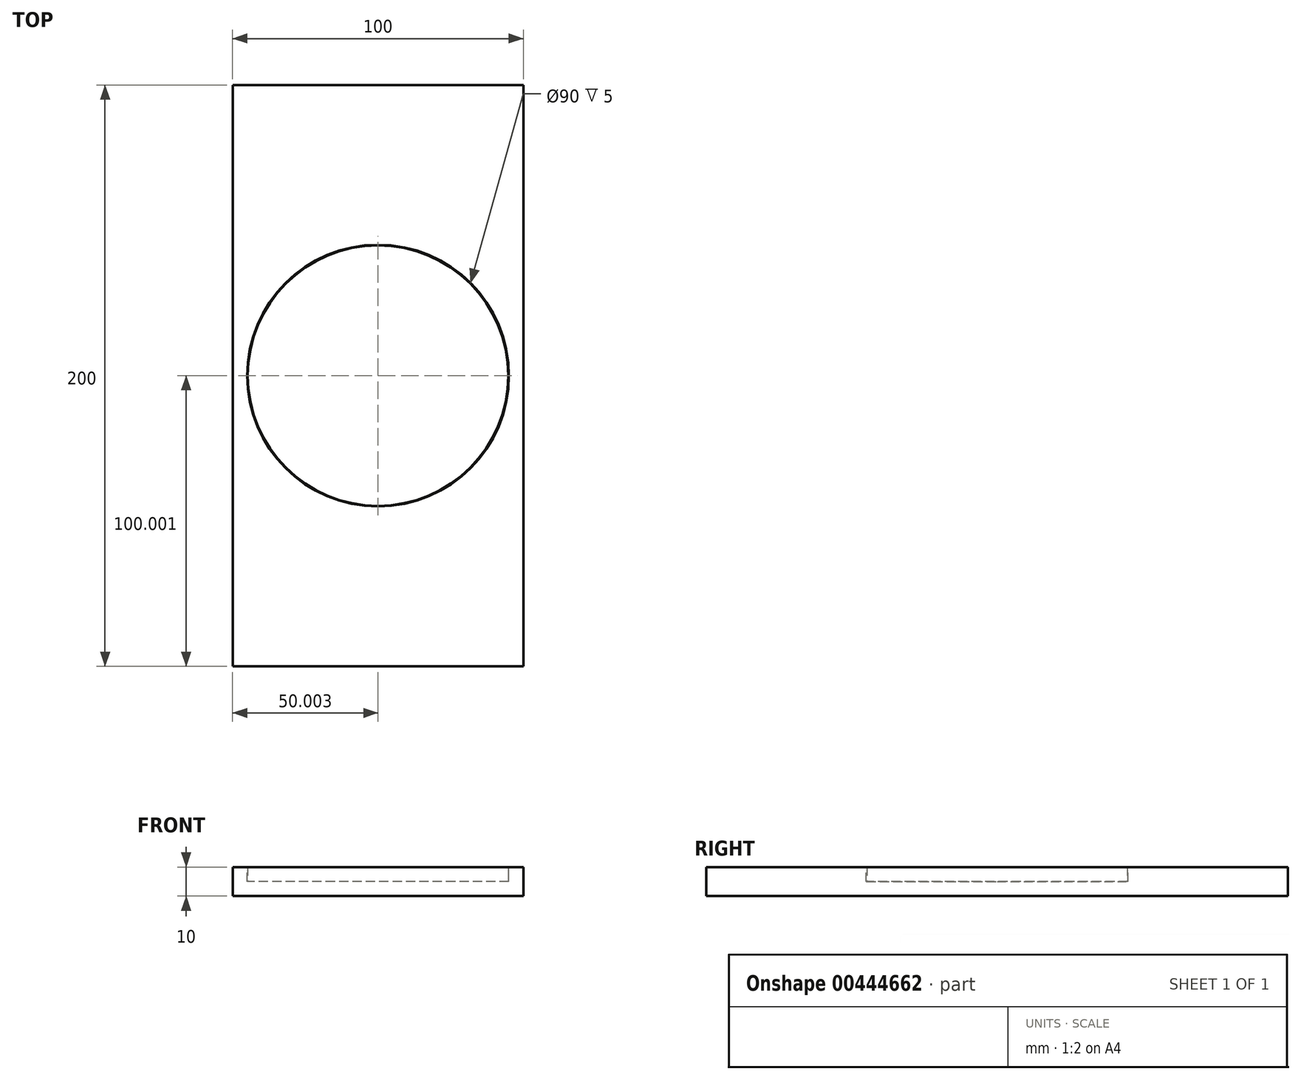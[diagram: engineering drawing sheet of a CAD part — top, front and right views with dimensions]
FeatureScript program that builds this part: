
annotation { "Feature Type Name" : "Feature", "Feature Type Description" : "" }
export const myFeature = defineFeature(function(context is Context, id is Id, definition is map)
    precondition{}
    {
        {
            var Q0;
            Q0=qCreatedBy(makeId("Top.planeOp"),FACE);
            var sketch = newSketch(context, id + "F0", { "sketchPlane" : qUnion([Q0])});
            skLineSegment(sketch, "E0.bottom", {"start": v(-48.37, 154.08) * mm, "end": v(51.63, 154.08) * mm});
            skLineSegment(sketch, "E0.top", {"start": v(-48.37, -45.92) * mm, "end": v(51.63, -45.92) * mm});
            skLineSegment(sketch, "E0.left", {"start": v(-48.37, 154.08) * mm, "end": v(-48.37, -45.92) * mm});
            skLineSegment(sketch, "E0.right", {"start": v(51.63, 154.08) * mm, "end": v(51.63, -45.92) * mm});
            skSolve(sketch);
        }
        {
            var Q0;
            Q0=makeQuery(id+"F0.imprint","IMPRINT",FACE,{"disambiguationData":[TD([[makeQuery(id+"F0.imprint","IMPRINT",EDGE,{"derivedFrom":sQuery(id+"F0.wireOp",EDGE,"E0.bottom")}),-1.0]])]});
            extrude(context, id + "F1", {"entities" : qUnion([Q0]), "depth" : 10 * mm});
        }
        {
            var Q0;
            Q0=makeQuery(id+"F1.opExtrude","CAP_FACE",FACE,{"disambiguationData":[OSD([sQuery(id+"F0.wireOp",EDGE,"E0.bottom"),sQuery(id+"F0.wireOp",EDGE,"E0.top"),sQuery(id+"F0.wireOp",EDGE,"E0.left"),sQuery(id+"F0.wireOp",EDGE,"E0.right")])],"isStart":false});
            var sketch = newSketch(context, id + "F2", { "sketchPlane" : qUnion([Q0])});
            skLineSegment(sketch, "E1", {"start": v(-48.37, 54.08) * mm, "end": v(51.63, 54.08) * mm, "construction": true});
            skCircle(sketch, "E2", {"center": v(1.63, 54.08) * mm, "radius": 45 * mm});
            skSolve(sketch);
        }
        {
            var Q0;
            Q0=makeQuery(id+"F2.imprint","IMPRINT",FACE,{"disambiguationData":[TD([[makeQuery(id+"F2.imprint","IMPRINT",EDGE,{"derivedFrom":sQuery(id+"F2.wireOp",EDGE,"E2")}),1.0]])]});
            extrude(context, id + "F3", {"entities" : qUnion([Q0]), "operationType" : NewBodyOperationType.REMOVE, "oppositeDirection" : true, "depth" : 5 * mm});
        }
        {
            var Q0;
            Q0=makeQuery(id+"F3.boolean.opBoolean","COPY",FACE,{"derivedFrom":makeQuery(id+"F3.opExtrude","CAP_FACE",FACE,{"disambiguationData":[OSD([sQuery(id+"F2.wireOp",EDGE,"E2")])],"isStart":false})});
            var sketch = newSketch(context, id + "F4", { "sketchPlane" : qUnion([Q0])});
            skCircle(sketch, "E3", {"center": v(1.63, 54.08) * mm, "radius": 44.8 * mm});
            skSolve(sketch);
        }
        {
            var Q0;
            Q0=makeQuery(id+"F4.imprint","IMPRINT",FACE,{"disambiguationData":[TD([[makeQuery(id+"F4.imprint","IMPRINT",EDGE,{"derivedFrom":sQuery(id+"F4.wireOp",EDGE,"E3")}),1.0]])]});
            extrude(context, id + "F5", {"entities" : qUnion([Q0]), "operationType" : NewBodyOperationType.ADD, "depth" : 5 * mm});
        }
    });
